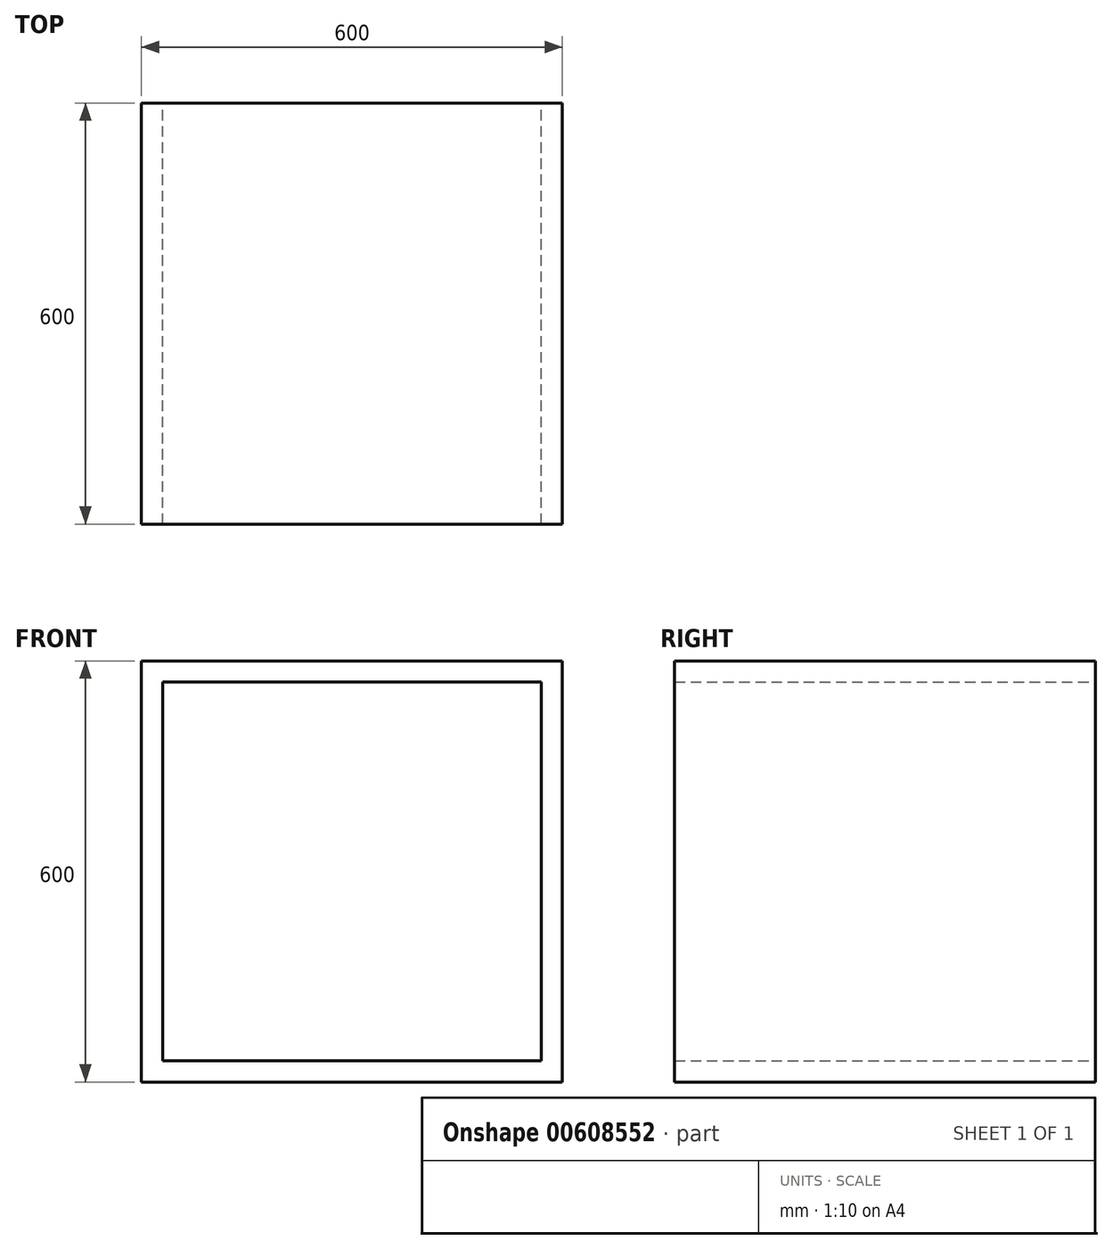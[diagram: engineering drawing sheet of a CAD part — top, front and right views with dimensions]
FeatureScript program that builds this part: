
annotation { "Feature Type Name" : "Feature", "Feature Type Description" : "" }
export const myFeature = defineFeature(function(context is Context, id is Id, definition is map)
    precondition{}
    {
        {
            assignVariable(context, id + "F0", {"name" : "depth", "anyValue" : 600});
        }
        {
            var Q0;
            Q0=qCreatedBy(makeId("Front.planeOp"),FACE);
            var sketch = newSketch(context, id + "F1", { "sketchPlane" : qUnion([Q0])});
            skLineSegment(sketch, "E0.bottom", {"start": v(300, -300) * mm, "end": v(-300, -300) * mm});
            skLineSegment(sketch, "E0.top", {"start": v(300, 300) * mm, "end": v(-300, 300) * mm});
            skLineSegment(sketch, "E0.left", {"start": v(300, -300) * mm, "end": v(300, 300) * mm});
            skLineSegment(sketch, "E0.right", {"start": v(-300, -300) * mm, "end": v(-300, 300) * mm});
            skPoint(sketch, "E0.middle", {"position": v(0, 0) * mm});
            skLineSegment(sketch, "E1.0", {"start": v(270, -270) * mm, "end": v(270, 270) * mm});
            skLineSegment(sketch, "E1.1", {"start": v(270, -270) * mm, "end": v(-270, -270) * mm});
            skLineSegment(sketch, "E1.2", {"start": v(-270, -270) * mm, "end": v(-270, 270) * mm});
            skLineSegment(sketch, "E1.3", {"start": v(270, 270) * mm, "end": v(-270, 270) * mm});
            skSolve(sketch);
        }
        {
            var Q0;
            Q0=makeQuery(id+"F1.imprint","IMPRINT",FACE,{"disambiguationData":[TD([[makeQuery(id+"F1.imprint","IMPRINT",EDGE,{"derivedFrom":sQuery(id+"F1.wireOp",EDGE,"E0.bottom")}),-1.0]])]});
            extrude(context, id + "F2", {"entities" : qUnion([Q0]), "depth" : getVariable(context, 'depth') * mm, "offsetDistance" : 25 * mm});
        }
    });
